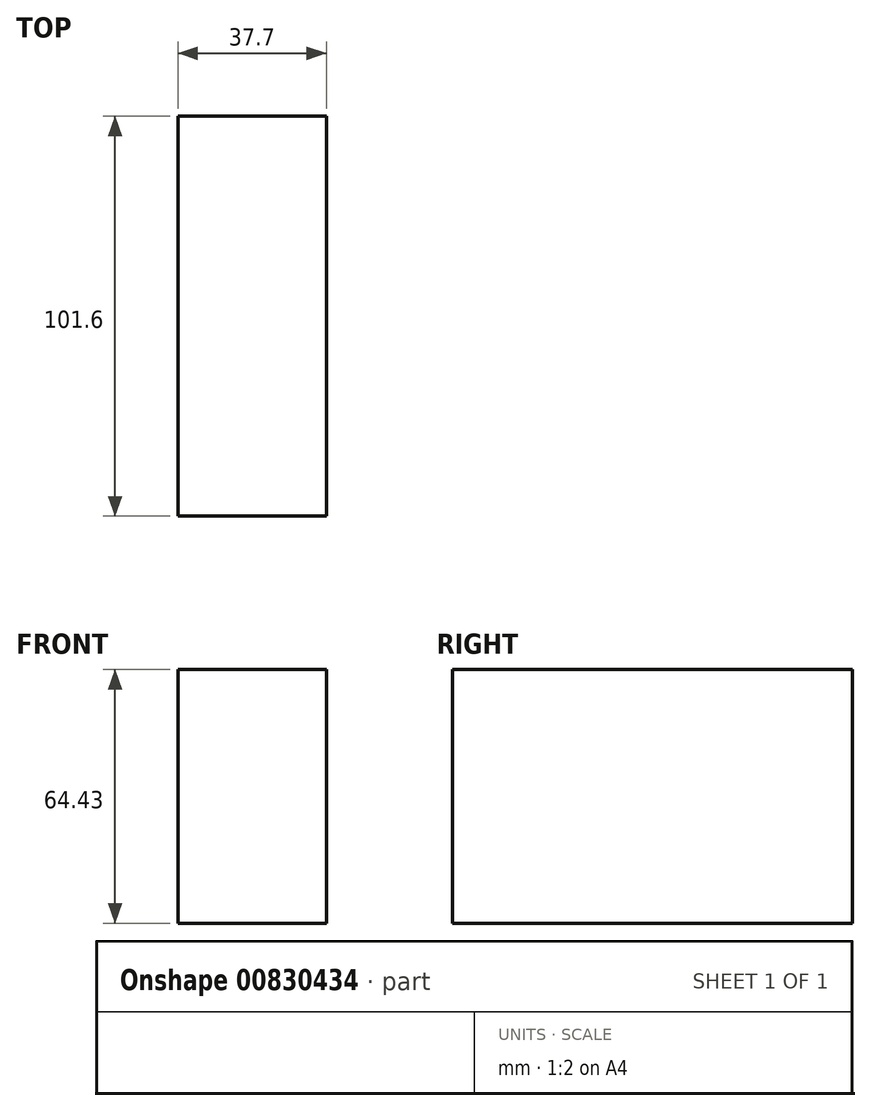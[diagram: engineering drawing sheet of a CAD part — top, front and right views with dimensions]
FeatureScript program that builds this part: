
annotation { "Feature Type Name" : "Feature", "Feature Type Description" : "" }
export const myFeature = defineFeature(function(context is Context, id is Id, definition is map)
    precondition{}
    {
        {
            var Q0;
            Q0=qCreatedBy(makeId("Front.planeOp"),FACE);
            var sketch = newSketch(context, id + "F0", { "sketchPlane" : qUnion([Q0])});
            skLineSegment(sketch, "E0.bottom", {"start": v(0, 0) * mm, "end": v(37.7, 0) * mm});
            skLineSegment(sketch, "E0.top", {"start": v(0, 64.43) * mm, "end": v(37.7, 64.43) * mm});
            skLineSegment(sketch, "E0.left", {"start": v(0, 0) * mm, "end": v(0, 64.43) * mm});
            skLineSegment(sketch, "E0.right", {"start": v(37.7, 0) * mm, "end": v(37.7, 64.43) * mm});
            skSolve(sketch);
        }
        {
            var Q0;
            Q0=makeQuery(id+"F0.imprint","IMPRINT",FACE,{"disambiguationData":[TD([[makeQuery(id+"F0.imprint","IMPRINT",EDGE,{"derivedFrom":sQuery(id+"F0.wireOp",EDGE,"E0.bottom")}),1.0]])]});
            extrude(context, id + "F1", {"entities" : qUnion([Q0]), "depth" : 101.6 * mm, "offsetDistance" : 25.4 * mm});
        }
    });
